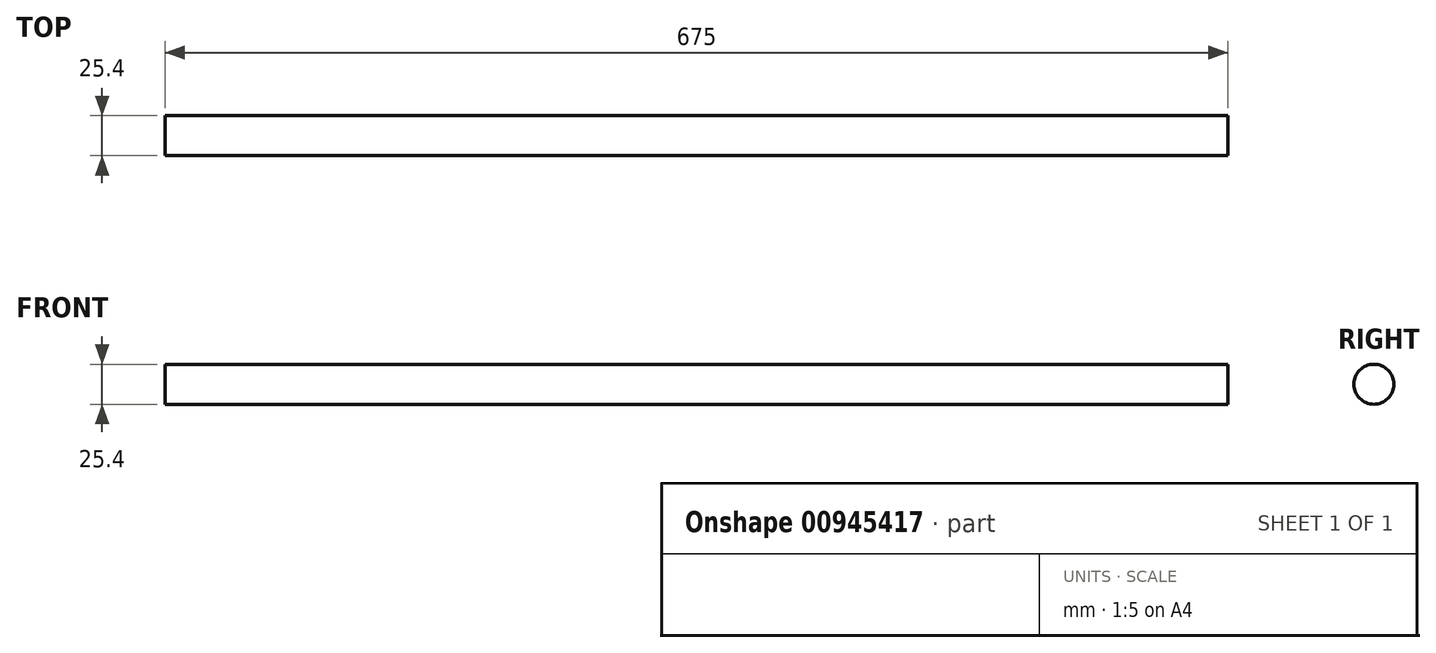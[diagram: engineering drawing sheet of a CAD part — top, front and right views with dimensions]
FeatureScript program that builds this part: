
annotation { "Feature Type Name" : "Feature", "Feature Type Description" : "" }
export const myFeature = defineFeature(function(context is Context, id is Id, definition is map)
    precondition{}
    {
        {
            var Q0;
            Q0=qCreatedBy(makeId("Right.planeOp"),FACE);
            var sketch = newSketch(context, id + "F0", { "sketchPlane" : qUnion([Q0])});
            skCircle(sketch, "E0", {"center": v(0, 0) * mm, "radius": 12.7 * mm});
            skSolve(sketch);
        }
        {
            var Q0;
            Q0=sQuery(id+"F0.wireOp",EDGE,"E0");
            extrude(context, id + "F1", {"bodyType" : ToolBodyType.SURFACE, "surfaceEntities" : qUnion([Q0]), "depth" : 675 * mm, "offsetDistance" : 25.4 * mm});
        }
    });
